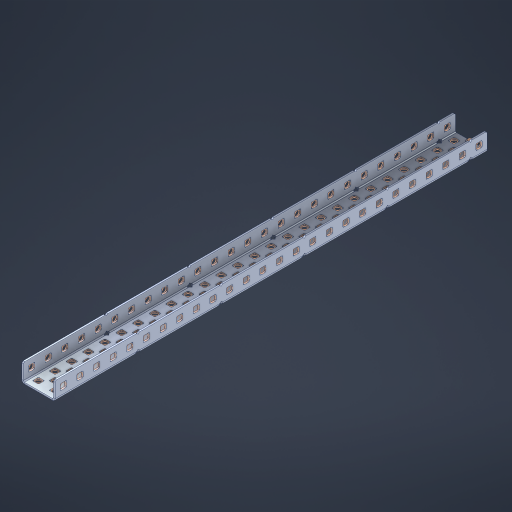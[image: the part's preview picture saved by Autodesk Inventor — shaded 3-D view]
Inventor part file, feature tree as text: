
AUTODESK INVENTOR PART (.ipt)
format: ipt  version: 2023 (Build 270158000, 158)  size: 1,693,184 bytes
history: native  units: in
note: dims shown in document units (in); Inventor stores cm internally (conversion verified against a paired STEP export)
features: other x137, extrude x128, sheet_metal_op x11, sketch x10, pattern_linear x2, mirror x1, chamfer x1
ambient origin geometry x8: Origin, YZ Plane, XZ Plane, XY Plane, X Axis, Y Axis, Z Axis, Center Point
bodies: Solid1 (feature_tree), Body (feature_tree)
feature tree (290):
  sheet_metal_op  "Flanges"
  other  "Flange Pattern Plane"
  other  "Flange Pattern Sketch"
  sheet_metal_op  "Flange Pattern"
  sheet_metal_op  "Body Pattern"
  pattern_linear  "Center Pattern"  Spacing1=0.0469in  [1 undecoded]
  other  "Arc Length"
  mirror  "Notch Mirror"
  pattern_linear  "Notch Pattern"  Spacing1=0.182in  [1 undecoded]
  chamfer  "End Chamfer"
  extrude  "Half Cut"  Depth=0.02in
  sketch  "Sketch1"  dims[d0=1.0in]
  other  "Plate1"
  sketch  "Sketch2"  dims[d1=13.0in]
  other  "Plate2"
  sheet_metal_op  "Bend1"
  sheet_metal_op  "Corner1"
  sketch  "Sketch3"  dims[d2=0.0469in]
  sketch  "Sketch7"  dims[d3=0.0469in]
  other  "Srf1"
  other  "Srf2"
  sketch  "Sketch8"  dims[d4=0.0234in]
  sketch  "Sketch9"  dims[d5=0.0938in]
  other  "Srf91"
  sheet_metal_op  "Body Pattern Sketch"
  other  "Srf92"
  sketch  "Sketch13"  dims[d6=0.0469in]
  sketch  "Sketch14"  dims[d7=0.5in d8=90.0deg d9=0.0312in]
  sketch  "Sketch15"  dims[d10=0.1875in]
  sketch  "Sketch16"  dims[d11=0.0469in d12=0.0469in d16=0.182in d17=0.02in d18=0.0469in d19=0.0in d20=0.25in d21=0.25in d38=10.2362in d40=0.5in d41=0.7874in d43=1.0in d46=0.172in d47=1.0in d48=0.0in d49=0.182in d50=0.02in d51=0.25in d52=0.25in d53=0.0469in d54=0.0in d55=0.172in d56=1.0in d57=0.0in d58=0.25in d60=10.2362in d62=0.5in d63=0.7874in d65=0.5in d85=0.1227in d86=0.1659in d88=0.04in d89=0.0469in d90=0.0in d91=0.04in d92=0.0491in d95=2.5in d96=0.04in d97=0.25in d98=45.0deg d99=0.25in d100=0.5in d101=0.0in d102=2.497in d106=0.182in d107=0.02in d108=0.5in d109=0.5in d110=0.0469in d111=0.0in d112=0.172in d113=0.5in d114=0.0in d117=0.5in d118=0.5in d119=0.5in]
  other  "Srf786"
  other  "Srf823"
  other  "Srf824"
  other  "Srf825"
  other  "Srf826"
  other  "Srf827"
  other  "Srf828"
  other  "Srf829"
  other  "Srf856"
  other  "Srf857"
  other  "Srf858"
  other  "Srf859"
  other  "Srf860"
  other  "Srf861"
  other  "Srf862"
  other  "Srf889"
  other  "Srf890"
  other  "Srf891"
  other  "Srf892"
  other  "Srf893"
  other  "Srf894"
  other  "Srf895"
  other  "Srf896"
  other  "Srf922"
  other  "Srf923"
  other  "Srf924"
  other  "Srf925"
  other  "Srf926"
  other  "Srf959"
  other  "Srf960"
  other  "Srf961"
  other  "Srf962"
  other  "Srf963"
  other  "Srf996"
  other  "Srf997"
  other  "Srf998"
  other  "Srf999"
  other  "Srf1000"
  other  "Srf1143"
  other  "Srf1144"
  other  "Srf1145"
  other  "Srf1146"
  other  "Srf1147"
  other  "Srf1148"
  other  "Srf1149"
  other  "Srf1150"
  other  "Srf1151"
  other  "Srf1152"
  other  "Srf1153"
  other  "Srf1154"
  other  "Srf1155"
  other  "Srf1156"
  other  "Srf1157"
  other  "Srf1158"
  other  "Srf1159"
  other  "Srf1160"
  other  "Srf1161"
  other  "Srf1162"
  other  "Srf1163"
  other  "Srf1164"
  other  "Srf1165"
  other  "Srf1166"
  other  "Srf1167"
  other  "Srf1168"
  other  "Srf1169"
  other  "Srf1170"
  other  "Srf1171"
  other  "Srf1172"
  other  "Srf1173"
  other  "Srf1174"
  other  "Srf1175"
  other  "Srf1176"
  other  "Srf1177"
  other  "Srf1178"
  other  "Srf1179"
  other  "Srf1180"
  other  "Srf1199"
  other  "Srf1200"
  other  "Srf1201"
  other  "Srf1202"
  other  "Srf1203"
  other  "Srf1204"
  other  "Srf1205"
  other  "Srf1206"
  other  "Srf1207"
  other  "Srf1208"
  other  "Srf1209"
  other  "Srf1210"
  other  "Srf1211"
  other  "Srf1212"
  other  "Srf1213"
  other  "Srf1214"
  other  "Srf1215"
  other  "Srf1216"
  other  "Srf1217"
  other  "Srf1218"
  other  "Srf1219"
  other  "Srf1220"
  other  "Srf1221"
  other  "Srf1222"
  other  "Srf1223"
  other  "Srf1224"
  other  "Srf1225"
  other  "Srf1226"
  other  "Srf1227"
  other  "Srf1228"
  other  "Srf1229"
  other  "Srf1230"
  other  "Srf1231"
  other  "Srf1232"
  other  "Srf1233"
  other  "Srf1234"
  other  "Srf1235"
  other  "Srf1236"
  other  "Srf1255"
  other  "Srf1256"
  other  "Srf1257"
  other  "Srf1258"
  other  "Srf1259"
  other  "Srf1260"
  other  "Srf1261"
  other  "Srf1262"
  other  "Srf1263"
  other  "Srf1264"
  other  "Srf1265"
  other  "Srf1266"
  sheet_metal_op  "Flange Stamp"
  sheet_metal_op  "Flange Circle"
  sheet_metal_op  "Body Stamp"
  sheet_metal_op  "Body Circle"
  other  "Center Stamp"
  other  "Center Circle"
  sheet_metal_op  "Notch"
  extrude  "ExtrusionSrf2"  Depth=0.0469in
  extrude  "ExtrusionSrf92"  TaperAngle=0.0deg  [1 undecoded]
  extrude  "ExtrusionSrf823"  Depth=0.5in
  extrude  "ExtrusionSrf824"  Depth=0.5in
  extrude  "ExtrusionSrf825"  Depth=0.5in
  extrude  "ExtrusionSrf826"  Depth=0.5in
  extrude  "ExtrusionSrf827"  Depth=1.0in TaperAngle=0.0deg
  extrude  "ExtrusionSrf828"  Depth=0.5in
  extrude  "ExtrusionSrf829"  Depth=0.02in
  extrude  "ExtrusionSrf856"  Depth=0.5in
  extrude  "ExtrusionSrf857"  Depth=0.5in
  extrude  "ExtrusionSrf858"  Depth=0.0469in
  extrude  "ExtrusionSrf859"  TaperAngle=0.0deg  [1 undecoded]
  extrude  "ExtrusionSrf860"  Depth=0.5in
  extrude  "ExtrusionSrf861"  Depth=1.0in TaperAngle=0.0deg
  extrude  "ExtrusionSrf862"  Depth=0.5in
  extrude  "ExtrusionSrf889"  Depth=0.5in
  extrude  "ExtrusionSrf890"  Depth=0.5in
  extrude  "ExtrusionSrf891"  Depth=0.5in
  extrude  "ExtrusionSrf892"  Depth=0.5in
  extrude  "ExtrusionSrf893"  Depth=0.5in
  extrude  "ExtrusionSrf894"  Depth=0.0469in
  extrude  "ExtrusionSrf895"  TaperAngle=0.0deg  [1 undecoded]
  extrude  "ExtrusionSrf896"  Depth=0.5in
  extrude  "ExtrusionSrf922"  Depth=0.5in
  extrude  "ExtrusionSrf923"  Depth=2.5in
  extrude  "ExtrusionSrf924"  Depth=0.5in TaperAngle=45.0deg
  extrude  "ExtrusionSrf925"  Depth=0.5in
  extrude  "ExtrusionSrf926"  Depth=0.5in TaperAngle=0.0deg
  extrude  "ExtrusionSrf959"  Depth=0.5in
  extrude  "ExtrusionSrf960"  Depth=0.5in
  extrude  "ExtrusionSrf961"  Depth=0.02in
  extrude  "ExtrusionSrf962"  Depth=0.5in
  extrude  "ExtrusionSrf963"  Depth=0.5in
  extrude  "ExtrusionSrf996"  Depth=0.0469in
  extrude  "ExtrusionSrf997"  TaperAngle=0.0deg  [1 undecoded]
  extrude  "ExtrusionSrf998"  Depth=0.5in
  extrude  "ExtrusionSrf999"  Depth=0.5in TaperAngle=0.0deg
  extrude  "ExtrusionSrf1000"  Depth=0.5in
  extrude  "ExtrusionSrf1143"  Depth=0.5in
  extrude  "ExtrusionSrf1144"  Depth=0.5in
  extrude  "ExtrusionSrf1145"  [1 undecoded]
  extrude  "ExtrusionSrf1146"  [1 undecoded]
  extrude  "ExtrusionSrf1147"  [1 undecoded]
  extrude  "ExtrusionSrf1148"  [1 undecoded]
  extrude  "ExtrusionSrf1149"  [1 undecoded]
  extrude  "ExtrusionSrf1150"  [1 undecoded]
  extrude  "ExtrusionSrf1151"  [1 undecoded]
  extrude  "ExtrusionSrf1152"  [1 undecoded]
  extrude  "ExtrusionSrf1153"  [1 undecoded]
  extrude  "ExtrusionSrf1154"  [1 undecoded]
  extrude  "ExtrusionSrf1155"  [1 undecoded]
  extrude  "ExtrusionSrf1156"  [1 undecoded]
  extrude  "ExtrusionSrf1157"  [1 undecoded]
  extrude  "ExtrusionSrf1158"  [1 undecoded]
  extrude  "ExtrusionSrf1159"  [1 undecoded]
  extrude  "ExtrusionSrf1160"  [1 undecoded]
  extrude  "ExtrusionSrf1161"  [1 undecoded]
  extrude  "ExtrusionSrf1162"  [1 undecoded]
  extrude  "ExtrusionSrf1163"  [1 undecoded]
  extrude  "ExtrusionSrf1164"  [1 undecoded]
  extrude  "ExtrusionSrf1165"  [1 undecoded]
  extrude  "ExtrusionSrf1166"  [1 undecoded]
  extrude  "ExtrusionSrf1167"  [1 undecoded]
  extrude  "ExtrusionSrf1168"  [1 undecoded]
  extrude  "ExtrusionSrf1169"  [1 undecoded]
  extrude  "ExtrusionSrf1170"  [1 undecoded]
  extrude  "ExtrusionSrf1171"  [1 undecoded]
  extrude  "ExtrusionSrf1172"  [1 undecoded]
  extrude  "ExtrusionSrf1173"  [1 undecoded]
  extrude  "ExtrusionSrf1174"  [1 undecoded]
  extrude  "ExtrusionSrf1175"  [1 undecoded]
  extrude  "ExtrusionSrf1176"  [1 undecoded]
  extrude  "ExtrusionSrf1177"  [1 undecoded]
  extrude  "ExtrusionSrf1178"  [1 undecoded]
  extrude  "ExtrusionSrf1179"  [1 undecoded]
  extrude  "ExtrusionSrf1180"  [1 undecoded]
  extrude  "ExtrusionSrf1199"  [1 undecoded]
  extrude  "ExtrusionSrf1200"  [1 undecoded]
  extrude  "ExtrusionSrf1201"  [1 undecoded]
  extrude  "ExtrusionSrf1202"  [1 undecoded]
  extrude  "ExtrusionSrf1203"  [1 undecoded]
  extrude  "ExtrusionSrf1204"  [1 undecoded]
  extrude  "ExtrusionSrf1205"  [1 undecoded]
  extrude  "ExtrusionSrf1206"  [1 undecoded]
  extrude  "ExtrusionSrf1207"  [1 undecoded]
  extrude  "ExtrusionSrf1208"  [1 undecoded]
  extrude  "ExtrusionSrf1209"  [1 undecoded]
  extrude  "ExtrusionSrf1210"  [1 undecoded]
  extrude  "ExtrusionSrf1211"  [1 undecoded]
  extrude  "ExtrusionSrf1212"  [1 undecoded]
  extrude  "ExtrusionSrf1213"  [1 undecoded]
  extrude  "ExtrusionSrf1214"  [1 undecoded]
  extrude  "ExtrusionSrf1215"  [1 undecoded]
  extrude  "ExtrusionSrf1216"  [1 undecoded]
  extrude  "ExtrusionSrf1217"  [1 undecoded]
  extrude  "ExtrusionSrf1218"  [1 undecoded]
  extrude  "ExtrusionSrf1219"  [1 undecoded]
  extrude  "ExtrusionSrf1220"  [1 undecoded]
  extrude  "ExtrusionSrf1221"  [1 undecoded]
  extrude  "ExtrusionSrf1222"  [1 undecoded]
  extrude  "ExtrusionSrf1223"  [1 undecoded]
  extrude  "ExtrusionSrf1224"  [1 undecoded]
  extrude  "ExtrusionSrf1225"  [1 undecoded]
  extrude  "ExtrusionSrf1226"  [1 undecoded]
  extrude  "ExtrusionSrf1227"  [1 undecoded]
  extrude  "ExtrusionSrf1228"  [1 undecoded]
  extrude  "ExtrusionSrf1229"  [1 undecoded]
  extrude  "ExtrusionSrf1230"  [1 undecoded]
  extrude  "ExtrusionSrf1231"  [1 undecoded]
  extrude  "ExtrusionSrf1232"  [1 undecoded]
  extrude  "ExtrusionSrf1233"  [1 undecoded]
  extrude  "ExtrusionSrf1234"  [1 undecoded]
  extrude  "ExtrusionSrf1235"  [1 undecoded]
  extrude  "ExtrusionSrf1236"  [1 undecoded]
  extrude  "ExtrusionSrf1255"  [1 undecoded]
  extrude  "ExtrusionSrf1256"  [1 undecoded]
  extrude  "ExtrusionSrf1257"  [1 undecoded]
  extrude  "ExtrusionSrf1258"  [1 undecoded]
  extrude  "ExtrusionSrf1259"  [1 undecoded]
  extrude  "ExtrusionSrf1260"  [1 undecoded]
  extrude  "ExtrusionSrf1261"  [1 undecoded]
  extrude  "ExtrusionSrf1262"  [1 undecoded]
  extrude  "ExtrusionSrf1263"  [1 undecoded]
  extrude  "ExtrusionSrf1264"  [1 undecoded]
  extrude  "ExtrusionSrf1265"  [1 undecoded]
  extrude  "ExtrusionSrf1266"  [1 undecoded]
note: 92 required parameter values undecoded (feature->parameter linkage not recoverable at this tier; creation-order binding heuristic only, values carry confidence <= 0.55)
